# Revit family: Hager-Orion_Plus-IP65-D250-Cl.I-Steel_encl-630A-CH-fr
name_source: partatom
category: Equipement électrique
units: mm (PartAtom-declared; Revit-internal decimal feet)

## family parameters
Configuration du panneau = Deux colonnes, circuits au sein
Cote de connecteur circulaire = Utiliser le diamètre
Couper avec des vides une fois chargée = Non
Hôte = Face
Partagée = Non
Point de calcul de pièce = Non
Type d'élément = Tableau de raccordement

## types (17) — shared parameters
Commentaires du type = Orion Plus
EF000003 - mode de pose = EV000384 - saillie
EF000007 - couleur = EV000270 - gris
EF000049 - profondeur = 250 mm  [stored 0.82021 ft]
EF000116 - numéro RAL = 7035
EF000118 - avec cadre/support de montage = Non
EF000437 - nombre d'entrées de conduit = 2
EF001596 - matériau du boîtier/corps = EV000179 - acier
EF001613 - maintien de fonction = EV000494 - sans
EF004293 - indice de protection contre les chocs (IK) = EV008784 - IK10
EF004464 - type de porte = EV002646 - unique
EF005474 - indice de protection (IP) = EV006421 - IP65
EF006306 - avec serrure = Oui
EF007800 - adapté à un parafoudre = Non
EF008873 - courant nominal (In) = 630 A
EF009171 - épaisseur de matériau de la porte/du couvercle = 2 mm  [stored 0.00656168 ft]
EF015940 - couvercle avec décharge de pression = Non
Fabricant = Hager
HG000002 - avec porte = Oui
HG000003 - Gamme = Orion Plus
HG000006 - Encastré = Non
HG000009 - Porte à double battant = Non
HG000010 - Portes asymétriques = Non
HG000023 - Armoire double section = Non
HG000024 - Hauteur de la section basse = 800 mm  [stored 2.62467 ft]
HG000026 - Installation au sol = Non
zero-valued in all types: EF000218 - profondeur d'encastrement, Elévation par défaut, HG000027 - Hauteur du socle

## per-type parameters (varying)
| type | EF000008 - largeur | EF000040 - hauteur | EF000266 - nombre de rangées | EF000339 - type de capot | EF001088 - possibilité de montage en saillie | EF001131 - profondeur intérieure | EF002950 - largeur en nombre de modules | EF003532 - convient pour utilisation à l’extérieur | EF004427 - nombre de modules | EF006244 - couvercle/porte transparent(e) | EF009170 - épaisseur de matériau du boîtier | EF009212 - finition du couvercle | EF009554 - nombre d'ouvertures pour plaques à bride | HG000004 - Référence fabricant |
| saillie IP65 L250 H600 P250  - FL166A | 250 mm  [stored 0.82021 ft] | 600 mm | 0 | EV004216 - porte | Non | 250 mm  [stored 0.82021 ft] | 0 | Non | 0 | Oui | 2 mm  [stored 0.00656168 ft] | EV009916 - avec échancrure | 0 | FL166A |
| saillie IP65 L400 H600 P250  - FL115A | 400 mm  [stored 1.31234 ft] | 600 mm | 0 | EV004216 - porte | Non | 250 mm  [stored 0.82021 ft] | 0 | Non | 0 | Non | 2 mm  [stored 0.00656168 ft] | EV009916 - avec échancrure | 2 | FL115A |
| saillie IP65 L400 H600 P250  - FL165A | 400 mm  [stored 1.31234 ft] | 600 mm | 0 | EV004216 - porte | Non | 250 mm  [stored 0.82021 ft] | 0 | Non | 0 | Oui | 2 mm  [stored 0.00656168 ft] | EV009916 - avec échancrure | 2 | FL165A |
| saillie IP65 L400 H650 P250  - FL118A | 400 mm  [stored 1.31234 ft] | 650 mm  [stored 2.13255 ft] | 4 | EV004216 - porte | Oui | 245 mm  [stored 0.803806 ft] | 16 | Non | 72 | Non | 2 mm  [stored 0.00656168 ft] | EV000116 - fermé | 2 | FL118A |
| saillie IP65 L400 H650 P250  - FL168A | 400 mm  [stored 1.31234 ft] | 650 mm  [stored 2.13255 ft] | 4 | EV004216 - porte | Oui | 245 mm  [stored 0.803806 ft] | 16 | Oui | 72 | Oui | 1 mm  [stored 0.00328084 ft] | EV000116 - fermé | 2 | FL168A |
| saillie IP65 L500 H650 P250  - FL120A | 500 mm  [stored 1.64042 ft] | 650 mm  [stored 2.13255 ft] | 4 | EV001012 - couvercle | Oui | 250 mm  [stored 0.82021 ft] | 22 | Non | 88 | Non | 2 mm  [stored 0.00656168 ft] | EV000116 - fermé | 2 | FL120A |
| saillie IP65 L500 H650 P250  - FL170A | 500 mm  [stored 1.64042 ft] | 650 mm  [stored 2.13255 ft] | 4 | EV004216 - porte | Oui | 200 mm  [stored 0.656168 ft] | 22 | Oui | 88 | Oui | 1 mm  [stored 0.00328084 ft] | EV000116 - fermé | 2 | FL170A |
| saillie IP65 L500 H800 P250  - FL122A | 500 mm  [stored 1.64042 ft] | 800 mm  [stored 2.62467 ft] | 5 | EV001012 - couvercle | Oui | 250 mm  [stored 0.82021 ft] | 22 | Non | 110 | Non | 2 mm  [stored 0.00656168 ft] | EV000116 - fermé | 2 | FL122A |
| saillie IP65 L500 H800 P250  - FL172A | 500 mm  [stored 1.64042 ft] | 800 mm  [stored 2.62467 ft] | 5 | EV004216 - porte | Oui | 250 mm  [stored 0.82021 ft] | 22 | Non | 110 | Oui | 1 mm  [stored 0.00328084 ft] | EV000116 - fermé | 2 | FL172A |
| saillie IP65 L600 H1250 P250  - FL179A | 600 mm | 1250 mm  [stored 4.10105 ft] | 8 | EV004216 - porte | Oui | 300 mm | 26 | Non | 208 | Oui | 1 mm  [stored 0.00328084 ft] | EV000116 - fermé | 2 | FL179A |
| saillie IP65 L600 H600 P250  - FL116A | 600 mm | 600 mm | 0 | EV004216 - porte | Non | 250 mm  [stored 0.82021 ft] | 0 | Non | 0 | Non | 2 mm  [stored 0.00656168 ft] | EV009916 - avec échancrure | 2 | FL116A |
| saillie IP65 L600 H800 P250  - FL123A | 600 mm | 800 mm  [stored 2.62467 ft] | 5 | EV001012 - couvercle | Oui | 250 mm  [stored 0.82021 ft] | 26 | Non | 130 | Non | 2 mm  [stored 0.00656168 ft] | EV000116 - fermé | 2 | FL123A |
| saillie IP65 L600 H800 P250  - FL173A | 600 mm | 800 mm  [stored 2.62467 ft] | 5 | EV004216 - porte | Oui | 250 mm  [stored 0.82021 ft] | 26 | Non | 130 | Oui | 1 mm  [stored 0.00328084 ft] | EV000116 - fermé | 2 | FL173A |
| saillie IP65 L600 H950 P250  - FL125A | 600 mm | 950 mm  [stored 3.1168 ft] | 6 | EV001012 - couvercle | Oui | 250 mm  [stored 0.82021 ft] | 26 | Non | 156 | Non | 2 mm  [stored 0.00656168 ft] | EV000116 - fermé | 2 | FL125A |
| saillie IP65 L600 H950 P250  - FL175A | 600 mm | 950 mm  [stored 3.1168 ft] | 6 | EV004216 - porte | Oui | 250 mm  [stored 0.82021 ft] | 26 | Non | 156 | Oui | 1 mm  [stored 0.00328084 ft] | EV000116 - fermé | 2 | FL175A |
| saillie IP65 L800 H950 P250  - FL127A | 800 mm  [stored 2.62467 ft] | 950 mm  [stored 3.1168 ft] | 6 | EV001012 - couvercle | Oui | 250 mm  [stored 0.82021 ft] | 37 | Non | 222 | Non | 2 mm  [stored 0.00656168 ft] | EV000116 - fermé | 2 | FL127A |
| saillie IP65 L800 H950 P250  - FL177A | 800 mm  [stored 2.62467 ft] | 950 mm  [stored 3.1168 ft] | 6 | EV004216 - porte | Oui | 250 mm  [stored 0.82021 ft] | 37 | Non | 222 | Oui | 1 mm  [stored 0.00328084 ft] | EV000116 - fermé | 2 | FL177A |

note: [stored X ft] marks values corroborated as IEEE doubles in the binary element streams (Revit-internal decimal feet)

## geometry (parser evidence)
native form markers: Sweep x7
no freeform markers — native parametric forms only
